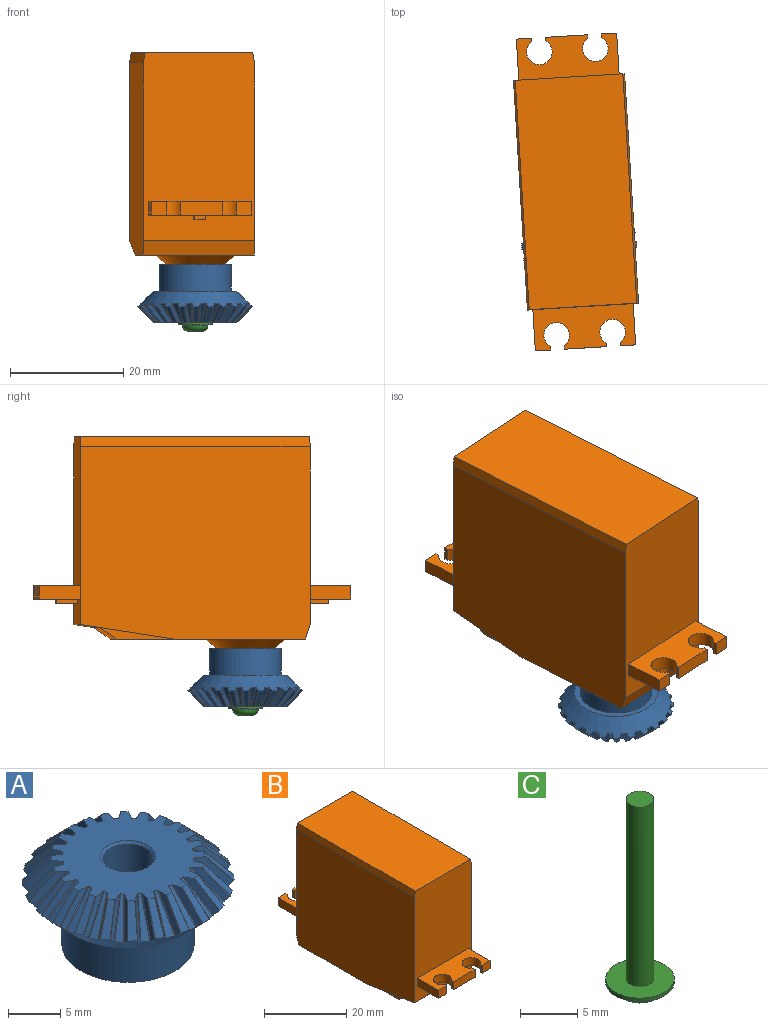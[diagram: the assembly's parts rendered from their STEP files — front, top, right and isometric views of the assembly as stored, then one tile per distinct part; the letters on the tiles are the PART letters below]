
ASSEMBLY  parts=3 mates=4
PART A: 200 faces, bbox 20.3x20.3x10.4 mm
  f0: cylinder r=0.05mm len=2.83mm, axis (0,-0.71,-0.71), area 0.2mm2, adj f1,f2,f181,f199
  f1: plane 3.76x3.28mm, normal (-0.94,-0.24,0.24), area 3.1mm2, adj f0,f3,f181,f199
  f2: cone r=10.16mm half-angle=45deg, axis (0,0,-1), area 3.1mm2, adj f0,f4,f181,f199
  f3: cylinder r=0.1mm len=3.37mm, axis (0,-0.71,-0.71), area 0.6mm2, adj f1,f5,f181,f199
  f4: cylinder r=0.05mm len=2.83mm, axis (-0.06,0.7,0.71), area 0.2mm2, adj f2,f6,f181,f199
  f5: cone r=5.83mm half-angle=45deg, axis (0,0,-1), area 2.7mm2, adj f3,f7,f181,f199
  f6: plane 3.77x3.28mm, normal (0.96,-0.16,0.24), area 3.1mm2, adj f4,f8,f181,f199
  f7: cylinder r=0.1mm len=3.37mm, axis (0.12,0.7,0.71), area 0.6mm2, adj f5,f9,f181,f199
  f8: cylinder r=0.1mm len=3.37mm, axis (-0.06,0.7,0.71), area 0.6mm2, adj f6,f10,f181,f199
  f9: plane 3.66x3.28mm, normal (0.88,-0.4,0.24), area 3.1mm2, adj f7,f11,f181,f199
  f10: cone r=5.83mm half-angle=45deg, axis (0,0,-1), area 2.7mm2, adj f8,f12,f181,f199
  f11: cylinder r=0.05mm len=2.83mm, axis (0.12,0.7,0.71), area 0.2mm2, adj f9,f13,f181,f199
  f12: cylinder r=0.1mm len=3.37mm, axis (0.18,-0.68,-0.71), area 0.6mm2, adj f10,f14,f181,f199
  f13: cone r=10.16mm half-angle=45deg, axis (0,0,-1), area 3.1mm2, adj f11,f15,f181,f199
  f14: plane 3.57x3.28mm, normal (-0.85,-0.48,0.24), area 3.1mm2, adj f12,f16,f181,f199
  f15: cylinder r=0.05mm len=2.83mm, axis (-0.18,-0.68,-0.71), area 0.2mm2, adj f13,f17,f181,f199
  f16: cylinder r=0.05mm len=2.83mm, axis (0.18,-0.68,-0.71), area 0.2mm2, adj f14,f18,f181,f199
  f17: plane 3.69x3.28mm, normal (-0.97,0.01,0.24), area 3.1mm2, adj f15,f19,f181,f199
  f18: cone r=10.16mm half-angle=45deg, axis (0,0,-1), area 3.1mm2, adj f16,f20,f181,f199
  f19: cylinder r=0.1mm len=3.37mm, axis (-0.18,-0.68,-0.71), area 0.6mm2, adj f17,f21,f181,f199
  f20: cylinder r=0.05mm len=2.83mm, axis (-0.24,0.66,0.71), area 0.2mm2, adj f18,f22,f181,f199
  f21: cone r=5.83mm half-angle=45deg, axis (0,0,-1), area 2.7mm2, adj f19,f23,f181,f199
  f22: plane 3.62x3.28mm, normal (0.97,0.09,0.24), area 3.1mm2, adj f20,f24,f181,f199
  f23: cylinder r=0.1mm len=3.37mm, axis (0.3,0.64,0.71), area 0.6mm2, adj f21,f25,f181,f199
  f24: cylinder r=0.1mm len=3.37mm, axis (-0.24,0.66,0.71), area 0.6mm2, adj f22,f26,f181,f199
  f25: plane 3.3x3.28mm, normal (0.75,-0.62,0.24), area 3.1mm2, adj f23,f27,f181,f199
  f26: cone r=5.83mm half-angle=45deg, axis (0,0,-1), area 2.7mm2, adj f24,f28,f181,f199
  f27: cylinder r=0.05mm len=2.83mm, axis (0.3,0.64,0.71), area 0.2mm2, adj f25,f29,f181,f199
  f28: cylinder r=0.1mm len=3.37mm, axis (0.35,-0.61,-0.71), area 0.6mm2, adj f26,f30,f181,f199
  f29: cone r=10.16mm half-angle=45deg, axis (0,0,-1), area 3.1mm2, adj f27,f31,f181,f199
  f30: plane 3.28x3.13mm, normal (-0.69,-0.68,0.24), area 3.1mm2, adj f28,f32,f181,f199
  f31: cylinder r=0.05mm len=2.83mm, axis (-0.35,-0.61,-0.71), area 0.2mm2, adj f29,f33,f181,f199
  f32: cylinder r=0.05mm len=2.83mm, axis (0.35,-0.61,-0.71), area 0.2mm2, adj f30,f34,f181,f199
  f33: plane 3.38x3.28mm, normal (-0.93,0.26,0.24), area 3.1mm2, adj f31,f35,f181,f199
  f34: cone r=10.16mm half-angle=45deg, axis (0,0,-1), area 3.1mm2, adj f32,f36,f181,f199
  f35: cylinder r=0.1mm len=3.37mm, axis (-0.35,-0.61,-0.71), area 0.6mm2, adj f33,f37,f181,f199
  f36: cylinder r=0.05mm len=2.83mm, axis (-0.41,0.58,0.71), area 0.2mm2, adj f34,f38,f181,f199
  f37: cone r=5.83mm half-angle=45deg, axis (0,0,-1), area 2.7mm2, adj f35,f39,f181,f199
  f38: plane 3.28x3.22mm, normal (0.91,0.34,0.24), area 3.1mm2, adj f36,f40,f181,f199
  f39: cylinder r=0.1mm len=3.37mm, axis (0.45,0.54,0.71), area 0.6mm2, adj f37,f41,f181,f199
  f40: cylinder r=0.1mm len=3.37mm, axis (-0.41,0.58,0.71), area 0.6mm2, adj f38,f42,f181,f199
  f41: plane 3.28x2.72mm, normal (0.56,-0.79,0.24), area 3.1mm2, adj f39,f43,f181,f199
  f42: cone r=5.83mm half-angle=45deg, axis (0,0,-1), area 2.7mm2, adj f40,f44,f181,f199
  f43: cylinder r=0.05mm len=2.83mm, axis (0.45,0.54,0.71), area 0.2mm2, adj f41,f45,f181,f199
  f44: cylinder r=0.1mm len=3.37mm, axis (0.5,-0.5,-0.71), area 0.6mm2, adj f42,f46,f181,f199
  f45: cone r=10.16mm half-angle=45deg, axis (0,0,-1), area 3.1mm2, adj f43,f47,f181,f199
  f46: plane 3.28x2.83mm, normal (-0.49,-0.84,0.24), area 3.1mm2, adj f44,f48,f181,f199
  f47: cylinder r=0.05mm len=2.83mm, axis (-0.5,-0.5,-0.71), area 0.2mm2, adj f45,f49,f181,f199
  f48: cylinder r=0.05mm len=2.83mm, axis (0.5,-0.5,-0.71), area 0.2mm2, adj f46,f50,f181,f199
  f49: plane 3.28x2.83mm, normal (-0.84,0.49,0.24), area 3.1mm2, adj f47,f51,f181,f199
  f50: cone r=10.16mm half-angle=45deg, axis (0,0,-1), area 3.1mm2, adj f48,f52,f181,f199
  f51: cylinder r=0.1mm len=3.37mm, axis (-0.5,-0.5,-0.71), area 0.6mm2, adj f49,f53,f181,f199
  f52: cylinder r=0.05mm len=2.83mm, axis (-0.54,0.45,0.71), area 0.2mm2, adj f50,f54,f181,f199
  f53: cone r=5.83mm half-angle=45deg, axis (0,0,-1), area 2.7mm2, adj f51,f55,f181,f199
  f54: plane 3.28x2.72mm, normal (0.79,0.56,0.24), area 3.1mm2, adj f52,f56,f181,f199
  f55: cylinder r=0.1mm len=3.37mm, axis (0.58,0.41,0.71), area 0.6mm2, adj f53,f57,f181,f199
  f56: cylinder r=0.1mm len=3.37mm, axis (-0.54,0.45,0.71), area 0.6mm2, adj f54,f58,f181,f199
  f57: plane 3.28x3.22mm, normal (0.34,-0.91,0.24), area 3.1mm2, adj f55,f59,f181,f199
  f58: cone r=5.83mm half-angle=45deg, axis (0,0,-1), area 2.7mm2, adj f56,f60,f181,f199
  f59: cylinder r=0.05mm len=2.83mm, axis (0.58,0.41,0.71), area 0.2mm2, adj f57,f61,f181,f199
  f60: cylinder r=0.1mm len=3.37mm, axis (0.61,-0.35,-0.71), area 0.6mm2, adj f58,f62,f181,f199
  f61: cone r=10.16mm half-angle=45deg, axis (0,0,-1), area 3.1mm2, adj f59,f63,f181,f199
  f62: plane 3.38x3.28mm, normal (-0.26,-0.93,0.24), area 3.1mm2, adj f60,f64,f181,f199
  f63: cylinder r=0.05mm len=2.83mm, axis (-0.61,-0.35,-0.71), area 0.2mm2, adj f61,f65,f181,f199
  f64: cylinder r=0.05mm len=2.83mm, axis (0.61,-0.35,-0.71), area 0.2mm2, adj f62,f66,f181,f199
  f65: plane 3.28x3.13mm, normal (-0.68,0.69,0.24), area 3.1mm2, adj f63,f67,f181,f199
  f66: cone r=10.16mm half-angle=45deg, axis (0,0,-1), area 3.1mm2, adj f64,f68,f181,f199
  f67: cylinder r=0.1mm len=3.37mm, axis (-0.61,-0.35,-0.71), area 0.6mm2, adj f65,f69,f181,f199
  f68: cylinder r=0.05mm len=2.83mm, axis (-0.64,0.3,0.71), area 0.2mm2, adj f66,f70,f181,f199
  f69: cone r=5.83mm half-angle=45deg, axis (0,0,-1), area 2.7mm2, adj f67,f71,f181,f199
  f70: plane 3.3x3.28mm, normal (0.62,0.75,0.24), area 3.1mm2, adj f68,f72,f181,f199
  f71: cylinder r=0.1mm len=3.37mm, axis (0.66,0.24,0.71), area 0.6mm2, adj f69,f73,f181,f199
  f72: cylinder r=0.1mm len=3.37mm, axis (-0.64,0.3,0.71), area 0.6mm2, adj f70,f74,f181,f199
  f73: plane 3.62x3.28mm, normal (0.09,-0.97,0.24), area 3.1mm2, adj f71,f75,f181,f199
  f74: cone r=5.83mm half-angle=45deg, axis (0,0,-1), area 2.7mm2, adj f72,f76,f181,f199
  f75: cylinder r=0.05mm len=2.83mm, axis (0.66,0.24,0.71), area 0.2mm2, adj f73,f77,f181,f199
  f76: cylinder r=0.1mm len=3.37mm, axis (0.68,-0.18,-0.71), area 0.6mm2, adj f74,f78,f181,f199
  f77: cone r=10.16mm half-angle=45deg, axis (0,0,-1), area 3.1mm2, adj f75,f79,f181,f199
  f78: plane 3.69x3.28mm, normal (-0.01,-0.97,0.24), area 3.1mm2, adj f76,f80,f181,f199
  f79: cylinder r=0.05mm len=2.83mm, axis (-0.68,-0.18,-0.71), area 0.2mm2, adj f77,f81,f181,f199
  f80: cylinder r=0.05mm len=2.83mm, axis (0.68,-0.18,-0.71), area 0.2mm2, adj f78,f82,f181,f199
  f81: plane 3.57x3.28mm, normal (-0.48,0.85,0.24), area 3.1mm2, adj f79,f83,f181,f199
  f82: cone r=10.16mm half-angle=45deg, axis (0,0,-1), area 3.1mm2, adj f80,f84,f181,f199
  f83: cylinder r=0.1mm len=3.37mm, axis (-0.68,-0.18,-0.71), area 0.6mm2, adj f81,f85,f181,f199
  f84: cylinder r=0.05mm len=2.83mm, axis (-0.7,0.12,0.71), area 0.2mm2, adj f82,f86,f181,f199
  f85: cone r=5.83mm half-angle=45deg, axis (0,0,-1), area 2.7mm2, adj f83,f87,f181,f199
  f86: plane 3.66x3.28mm, normal (0.4,0.88,0.24), area 3.1mm2, adj f84,f88,f181,f199
  f87: cylinder r=0.1mm len=3.37mm, axis (0.7,0.06,0.71), area 0.6mm2, adj f85,f89,f181,f199
  f88: cylinder r=0.1mm len=3.37mm, axis (-0.7,0.12,0.71), area 0.6mm2, adj f86,f90,f181,f199
  f89: plane 3.77x3.28mm, normal (-0.16,-0.96,0.24), area 3.1mm2, adj f87,f91,f181,f199
  f90: cone r=5.83mm half-angle=45deg, axis (0,0,-1), area 2.7mm2, adj f88,f92,f181,f199
  f91: cylinder r=0.05mm len=2.83mm, axis (0.7,0.06,0.71), area 0.2mm2, adj f89,f93,f181,f199
  f92: cylinder r=0.1mm len=3.37mm, axis (0.71,0,-0.71), area 0.6mm2, adj f90,f94,f181,f199
  f93: cone r=10.16mm half-angle=45deg, axis (0,0,-1), area 3.1mm2, adj f91,f95,f181,f199
  f94: plane 3.76x3.28mm, normal (0.24,-0.94,0.24), area 3.1mm2, adj f92,f96,f181,f199
  f95: cylinder r=0.05mm len=2.83mm, axis (-0.71,0,-0.71), area 0.2mm2, adj f93,f97,f181,f199
  f96: cylinder r=0.05mm len=2.83mm, axis (0.71,0,-0.71), area 0.2mm2, adj f94,f98,f181,f199
  f97: plane 3.76x3.28mm, normal (-0.24,0.94,0.24), area 3.1mm2, adj f95,f99,f181,f199
  f98: cone r=10.16mm half-angle=45deg, axis (0,0,-1), area 3.1mm2, adj f96,f100,f181,f199
  f99: cylinder r=0.1mm len=3.37mm, axis (-0.71,0,-0.71), area 0.6mm2, adj f97,f101,f181,f199
  f100: cylinder r=0.05mm len=2.83mm, axis (-0.7,-0.06,0.71), area 0.2mm2, adj f98,f102,f181,f199
  f101: cone r=5.83mm half-angle=45deg, axis (0,0,-1), area 2.7mm2, adj f99,f103,f181,f199
  f102: plane 3.77x3.28mm, normal (0.16,0.96,0.24), area 3.1mm2, adj f100,f104,f181,f199
  f103: cylinder r=0.1mm len=3.37mm, axis (0.7,-0.12,0.71), area 0.6mm2, adj f101,f105,f181,f199
  f104: cylinder r=0.1mm len=3.37mm, axis (-0.7,-0.06,0.71), area 0.6mm2, adj f102,f106,f181,f199
  f105: plane 3.66x3.28mm, normal (-0.4,-0.88,0.24), area 3.1mm2, adj f103,f107,f181,f199
  f106: cone r=5.83mm half-angle=45deg, axis (0,0,-1), area 2.7mm2, adj f104,f108,f181,f199
  f107: cylinder r=0.05mm len=2.83mm, axis (0.7,-0.12,0.71), area 0.2mm2, adj f105,f109,f181,f199
  f108: cylinder r=0.1mm len=3.37mm, axis (0.68,0.18,-0.71), area 0.6mm2, adj f106,f110,f181,f199
  f109: cone r=10.16mm half-angle=45deg, axis (0,0,-1), area 3.1mm2, adj f107,f111,f181,f199
  f110: plane 3.57x3.28mm, normal (0.48,-0.85,0.24), area 3.1mm2, adj f108,f112,f181,f199
  f111: cylinder r=0.05mm len=2.83mm, axis (-0.68,0.18,-0.71), area 0.2mm2, adj f109,f113,f181,f199
  f112: cylinder r=0.05mm len=2.83mm, axis (0.68,0.18,-0.71), area 0.2mm2, adj f110,f114,f181,f199
  f113: plane 3.69x3.28mm, normal (0.01,0.97,0.24), area 3.1mm2, adj f111,f115,f181,f199
  f114: cone r=10.16mm half-angle=45deg, axis (0,0,-1), area 3.1mm2, adj f112,f116,f181,f199
  f115: cylinder r=0.1mm len=3.37mm, axis (-0.68,0.18,-0.71), area 0.6mm2, adj f113,f117,f181,f199
  f116: cylinder r=0.05mm len=2.83mm, axis (-0.66,-0.24,0.71), area 0.2mm2, adj f114,f118,f181,f199
  f117: cone r=5.83mm half-angle=45deg, axis (0,0,-1), area 2.7mm2, adj f115,f119,f181,f199
  f118: plane 3.62x3.28mm, normal (-0.09,0.97,0.24), area 3.1mm2, adj f116,f120,f181,f199
  f119: cylinder r=0.1mm len=3.37mm, axis (0.64,-0.3,0.71), area 0.6mm2, adj f117,f121,f181,f199
  f120: cylinder r=0.1mm len=3.37mm, axis (-0.66,-0.24,0.71), area 0.6mm2, adj f118,f122,f181,f199
  f121: plane 3.3x3.28mm, normal (-0.62,-0.75,0.24), area 3.1mm2, adj f119,f123,f181,f199
  f122: cone r=5.83mm half-angle=45deg, axis (0,0,-1), area 2.7mm2, adj f120,f124,f181,f199
  f123: cylinder r=0.05mm len=2.83mm, axis (0.64,-0.3,0.71), area 0.2mm2, adj f121,f125,f181,f199
  f124: cylinder r=0.1mm len=3.37mm, axis (0.61,0.35,-0.71), area 0.6mm2, adj f122,f126,f181,f199
  f125: cone r=10.16mm half-angle=45deg, axis (0,0,-1), area 3.1mm2, adj f123,f127,f181,f199
  f126: plane 3.28x3.13mm, normal (0.68,-0.69,0.24), area 3.1mm2, adj f124,f128,f181,f199
  f127: cylinder r=0.05mm len=2.83mm, axis (-0.61,0.35,-0.71), area 0.2mm2, adj f125,f129,f181,f199
  f128: cylinder r=0.05mm len=2.83mm, axis (0.61,0.35,-0.71), area 0.2mm2, adj f126,f130,f181,f199
  f129: plane 3.38x3.28mm, normal (0.26,0.93,0.24), area 3.1mm2, adj f127,f131,f181,f199
  f130: cone r=10.16mm half-angle=45deg, axis (0,0,-1), area 3.1mm2, adj f128,f132,f181,f199
  f131: cylinder r=0.1mm len=3.37mm, axis (-0.61,0.35,-0.71), area 0.6mm2, adj f129,f133,f181,f199
  f132: cylinder r=0.05mm len=2.83mm, axis (-0.58,-0.41,0.71), area 0.2mm2, adj f130,f134,f181,f199
  f133: cone r=5.83mm half-angle=45deg, axis (0,0,-1), area 2.7mm2, adj f131,f135,f181,f199
  f134: plane 3.28x3.22mm, normal (-0.34,0.91,0.24), area 3.1mm2, adj f132,f136,f181,f199
  f135: cylinder r=0.1mm len=3.37mm, axis (0.54,-0.45,0.71), area 0.6mm2, adj f133,f137,f181,f199
  f136: cylinder r=0.1mm len=3.37mm, axis (-0.58,-0.41,0.71), area 0.6mm2, adj f134,f138,f181,f199
  f137: plane 3.28x2.72mm, normal (-0.79,-0.56,0.24), area 3.1mm2, adj f135,f139,f181,f199
  f138: cone r=5.83mm half-angle=45deg, axis (0,0,-1), area 2.7mm2, adj f136,f140,f181,f199
  f139: cylinder r=0.05mm len=2.83mm, axis (0.54,-0.45,0.71), area 0.2mm2, adj f137,f141,f181,f199
  f140: cylinder r=0.1mm len=3.37mm, axis (0.5,0.5,-0.71), area 0.6mm2, adj f138,f142,f181,f199
  f141: cone r=10.16mm half-angle=45deg, axis (0,0,-1), area 3.1mm2, adj f139,f143,f181,f199
  f142: plane 3.28x2.83mm, normal (0.84,-0.49,0.24), area 3.1mm2, adj f140,f144,f181,f199
  f143: cylinder r=0.05mm len=2.83mm, axis (-0.5,0.5,-0.71), area 0.2mm2, adj f141,f145,f181,f199
  f144: cylinder r=0.05mm len=2.83mm, axis (0.5,0.5,-0.71), area 0.2mm2, adj f142,f146,f181,f199
  f145: plane 3.28x2.83mm, normal (0.49,0.84,0.24), area 3.1mm2, adj f143,f147,f181,f199
  f146: cone r=10.16mm half-angle=45deg, axis (0,0,-1), area 3.1mm2, adj f144,f148,f181,f199
  f147: cylinder r=0.1mm len=3.37mm, axis (-0.5,0.5,-0.71), area 0.6mm2, adj f145,f149,f181,f199
  f148: cylinder r=0.05mm len=2.83mm, axis (-0.45,-0.54,0.71), area 0.2mm2, adj f146,f150,f181,f199
  f149: cone r=5.83mm half-angle=45deg, axis (0,0,-1), area 2.7mm2, adj f147,f151,f181,f199
  f150: plane 3.28x2.72mm, normal (-0.56,0.79,0.24), area 3.1mm2, adj f148,f152,f181,f199
  f151: cylinder r=0.1mm len=3.37mm, axis (0.41,-0.58,0.71), area 0.6mm2, adj f149,f153,f181,f199
  f152: cylinder r=0.1mm len=3.37mm, axis (-0.45,-0.54,0.71), area 0.6mm2, adj f150,f154,f181,f199
  f153: plane 3.28x3.22mm, normal (-0.91,-0.34,0.24), area 3.1mm2, adj f151,f155,f181,f199
  f154: cone r=5.83mm half-angle=45deg, axis (0,0,-1), area 2.7mm2, adj f152,f156,f181,f199
  f155: cylinder r=0.05mm len=2.83mm, axis (0.41,-0.58,0.71), area 0.2mm2, adj f153,f157,f181,f199
  f156: cylinder r=0.1mm len=3.37mm, axis (0.35,0.61,-0.71), area 0.6mm2, adj f154,f158,f181,f199
  f157: cone r=10.16mm half-angle=45deg, axis (0,0,-1), area 3.1mm2, adj f155,f159,f181,f199
  f158: plane 3.38x3.28mm, normal (0.93,-0.26,0.24), area 3.1mm2, adj f156,f160,f181,f199
  f159: cylinder r=0.05mm len=2.83mm, axis (-0.35,0.61,-0.71), area 0.2mm2, adj f157,f161,f181,f199
  f160: cylinder r=0.05mm len=2.83mm, axis (0.35,0.61,-0.71), area 0.2mm2, adj f158,f162,f181,f199
  f161: plane 3.28x3.13mm, normal (0.69,0.68,0.24), area 3.1mm2, adj f159,f163,f181,f199
  f162: cone r=10.16mm half-angle=45deg, axis (0,0,-1), area 3.1mm2, adj f160,f164,f181,f199
  f163: cylinder r=0.1mm len=3.37mm, axis (-0.35,0.61,-0.71), area 0.6mm2, adj f161,f165,f181,f199
  f164: cylinder r=0.05mm len=2.83mm, axis (-0.3,-0.64,0.71), area 0.2mm2, adj f162,f166,f181,f199
  f165: cone r=5.83mm half-angle=45deg, axis (0,0,-1), area 2.7mm2, adj f163,f167,f181,f199
  f166: plane 3.3x3.28mm, normal (-0.75,0.62,0.24), area 3.1mm2, adj f164,f168,f181,f199
  f167: cylinder r=0.1mm len=3.37mm, axis (0.24,-0.66,0.71), area 0.6mm2, adj f165,f169,f181,f199
  f168: cylinder r=0.1mm len=3.37mm, axis (-0.3,-0.64,0.71), area 0.6mm2, adj f166,f170,f181,f199
  f169: plane 3.62x3.28mm, normal (-0.97,-0.09,0.24), area 3.1mm2, adj f167,f171,f181,f199
  f170: cone r=5.83mm half-angle=45deg, axis (0,0,-1), area 2.7mm2, adj f168,f172,f181,f199
  f171: cylinder r=0.05mm len=2.83mm, axis (0.24,-0.66,0.71), area 0.2mm2, adj f169,f173,f181,f199
  f172: cylinder r=0.1mm len=3.37mm, axis (0.18,0.68,-0.71), area 0.6mm2, adj f170,f174,f181,f199
  f173: cone r=10.16mm half-angle=45deg, axis (0,0,-1), area 3.1mm2, adj f171,f175,f181,f199
  f174: plane 3.69x3.28mm, normal (0.97,-0.01,0.24), area 3.1mm2, adj f172,f176,f181,f199
  f175: cylinder r=0.05mm len=2.83mm, axis (-0.18,0.68,-0.71), area 0.2mm2, adj f173,f177,f181,f199
  f176: cylinder r=0.05mm len=2.83mm, axis (0.18,0.68,-0.71), area 0.2mm2, adj f174,f178,f181,f199
  f177: plane 3.57x3.28mm, normal (0.85,0.48,0.24), area 3.1mm2, adj f175,f179,f181,f199
  f178: cone r=10.16mm half-angle=45deg, axis (0,0,-1), area 3.1mm2, adj f176,f180,f181,f199
  f179: cylinder r=0.1mm len=3.37mm, axis (-0.18,0.68,-0.71), area 0.6mm2, adj f177,f181,f182,f199
  f180: cylinder r=0.05mm len=2.83mm, axis (-0.12,-0.7,0.71), area 0.2mm2, adj f178,f181,f183,f199
  f181: cone r=10.16mm half-angle=45deg, axis (0,0,1), area 192.1mm2, adj f0,f1,f2,f3,f4,f5,f6,f7
  f182: cone r=5.83mm half-angle=45deg, axis (0,0,-1), area 2.7mm2, adj f179,f181,f185,f199
  f183: plane 3.66x3.28mm, normal (-0.88,0.4,0.24), area 3.1mm2, adj f180,f181,f186,f199
  f184: plane 14.76x14.76mm, normal (0,0,-1), area 44.5mm2, adj f181,f187
  f185: cylinder r=0.1mm len=3.37mm, axis (0.06,-0.7,0.71), area 0.6mm2, adj f181,f182,f188,f199
  f186: cylinder r=0.1mm len=3.37mm, axis (-0.12,-0.7,0.71), area 0.6mm2, adj f181,f183,f189,f199
  f187: cylinder r=6.35mm len=12.7mm, axis (0,0,1), area 190mm2, adj f184,f190
  f188: plane 3.77x3.28mm, normal (-0.96,0.16,0.24), area 3.1mm2, adj f181,f185,f191,f199
  f189: cone r=5.83mm half-angle=45deg, axis (0,0,-1), area 2.7mm2, adj f181,f186,f192,f199
  f190: plane 12.7x12.7mm, normal (0,0,-1), area 105mm2, adj f187,f193
  f191: cylinder r=0.05mm len=2.83mm, axis (0.06,-0.7,0.71), area 0.2mm2, adj f181,f188,f194,f199
  f192: cylinder r=0.1mm len=3.37mm, axis (0,0.71,-0.71), area 0.6mm2, adj f181,f189,f195,f199
  f193: cone r=2.63mm half-angle=45deg, axis (0,0,-1), area 5.6mm2, adj f190,f196
  f194: cone r=10.16mm half-angle=45deg, axis (0,0,-1), area 3.1mm2, adj f181,f191,f197,f199
  f195: plane 3.76x3.28mm, normal (0.94,0.24,0.24), area 3.1mm2, adj f181,f192,f197,f199
  f196: cylinder r=2.37mm len=9.81mm, axis (0,0,-1), area 146.4mm2, adj f193,f198
  f197: cylinder r=0.05mm len=2.83mm, axis (0,0.71,-0.71), area 0.2mm2, adj f181,f194,f195,f199
  f198: cone r=2.63mm half-angle=45deg, axis (0,0,1), area 5.6mm2, adj f196,f199
  f199: plane 14.79x14.79mm, normal (0,0,1), area 128.5mm2, adj f0,f1,f2,f3,f4,f5,f6,f7
PART B: 51 faces, bbox 19.7x55.3x37.4 mm
  f0: plane 17.78x7.32mm, normal (0,0,-1), area 89.1mm2, adj f2,f3,f4,f12,f39,f40,f41,f42
  f1: plane 17.78x7.32mm, normal (0,0,1), area 96.4mm2, adj f2,f3,f4,f12,f39,f40,f41,f42
  f2: plane 2.71x2.41mm, normal (0,-1,0), area 6.5mm2, adj f0,f1,f40,f44
  f3: plane 7.49x2.41mm, normal (0,-1,0), area 18.1mm2, adj f0,f1,f41,f46
  f4: plane 2.71x2.41mm, normal (0,-1,0), area 6.5mm2, adj f0,f1,f39,f43
  f5: plane 33.22x19.69mm, normal (0,1,0), area 608.9mm2, adj f6,f11,f13,f14,f15,f16,f21,f25
  f6: plane 17.78x7.32mm, normal (0,0,-1), area 89.1mm2, adj f5,f7,f8,f25,f27,f28,f29,f30
  f7: plane 2.71x2.41mm, normal (0,1,0), area 6.5mm2, adj f6,f26,f27,f32
  f8: plane 7.49x2.41mm, normal (0,1,0), area 18.1mm2, adj f6,f26,f29,f33
  f9: plane 33.49x19.69mm, normal (0,0,-1), area 479.4mm2, adj f10,f11,f13,f17,f18,f19,f21,f22
  f10: plane 19.69x16.51mm, normal (0,-0.15,-0.99), area 92.1mm2, adj f9,f11,f12,f13,f17,f18,f19
  f11: plane 40.64x33.99mm, normal (-1,0,0), area 1358.9mm2, adj f5,f9,f10,f12,f16,f21
  f12: plane 33.19x19.69mm, normal (0,-1,0), area 608.3mm2, adj f0,f1,f10,f11,f13,f14,f15,f16
  f13: plane 40.64x33.99mm, normal (1,0,0), area 1358.9mm2, adj f5,f9,f10,f12,f15,f21
  f14: plane 40.64x19.06mm, normal (0,0,1), area 774.5mm2, adj f5,f12,f15,f16
  f15: plane 40.64x1.78mm, normal (0.98,0,0.17), area 73.4mm2, adj f5,f12,f13,f14
  f16: plane 40.64x1.78mm, normal (-0.98,0,0.17), area 73.4mm2, adj f5,f11,f12,f14
  f17: plane 13.07x2.03mm, normal (-1,0,0), area 10.3mm2, adj f9,f10,f19
  f18: plane 13.07x2.03mm, normal (1,0,0), area 10.3mm2, adj f9,f10,f19
  f19: plane 17.91x2.91mm, normal (0,-0.57,-0.82), area 63.5mm2, adj f9,f10,f17,f18
  f20: plane 10.16x10.16mm, normal (0,0,-1), area 53.6mm2, adj f22,f23
  f21: plane 19.69x2.54mm, normal (0,0.95,-0.3), area 52.4mm2, adj f5,f9,f11,f13
  f22: cone r=5.08mm half-angle=52.2deg, axis (0,0,1), area 102.1mm2, adj f9,f20
  f23: cylinder r=2.96mm len=10mm, axis (0,0,-1), area 185.9mm2, adj f20,f24
  f24: plane 5.92x5.92mm, normal (0,0,-1), area 27.5mm2, adj f23
  f25: plane 7.32x2.41mm, normal (-1,0,0), area 17.7mm2, adj f5,f6,f26,f28
  f26: plane 17.78x7.32mm, normal (0,0,1), area 96.4mm2, adj f5,f7,f8,f25,f27,f28,f29,f30
  f27: plane 7.32x2.41mm, normal (1,0,0), area 17.7mm2, adj f5,f6,f7,f26
  f28: plane 2.71x2.41mm, normal (0,1,0), area 6.5mm2, adj f6,f25,f26,f30
  f29: plane 2.41x0.64mm, normal (-1,0,0), area 1.5mm2, adj f6,f8,f26,f31
  f30: plane 2.41x0.64mm, normal (1,0,0), area 1.5mm2, adj f6,f26,f28,f31
  f31: cylinder r=2.25mm len=4.5mm, axis (0,0,-1), area 27.9mm2, adj f6,f26,f29,f30
  f32: plane 2.41x0.64mm, normal (-1,0,0), area 1.5mm2, adj f6,f7,f26,f34
  f33: plane 2.41x0.64mm, normal (1,0,0), area 1.5mm2, adj f6,f8,f26,f34
  f34: cylinder r=2.25mm len=4.5mm, axis (0,0,-1), area 27.9mm2, adj f6,f26,f32,f33
  f35: plane 3.81x0.86mm, normal (1,0,0), area 3.3mm2, adj f5,f6,f37,f38
  f36: plane 3.81x0.86mm, normal (-1,0,0), area 3.3mm2, adj f5,f6,f37,f38
  f37: plane 1.91x0.86mm, normal (0,1,0), area 1.6mm2, adj f6,f35,f36,f38
  f38: plane 3.81x1.91mm, normal (0,0,-1), area 7.3mm2, adj f5,f35,f36,f37
  f39: plane 7.32x2.41mm, normal (-1,0,0), area 17.7mm2, adj f0,f1,f4,f12
  f40: plane 7.32x2.41mm, normal (1,0,0), area 17.7mm2, adj f0,f1,f2,f12
  f41: plane 2.41x0.64mm, normal (-1,0,0), area 1.5mm2, adj f0,f1,f3,f42
  f42: cylinder r=2.25mm len=4.5mm, axis (0,0,-1), area 27.9mm2, adj f0,f1,f41,f43
  f43: plane 2.41x0.64mm, normal (1,0,0), area 1.5mm2, adj f0,f1,f4,f42
  f44: plane 2.41x0.64mm, normal (-1,0,0), area 1.5mm2, adj f0,f1,f2,f45
  f45: cylinder r=2.25mm len=4.5mm, axis (0,0,-1), area 27.9mm2, adj f0,f1,f44,f46
  f46: plane 2.41x0.64mm, normal (1,0,0), area 1.5mm2, adj f0,f1,f3,f45
  f47: plane 3.81x0.86mm, normal (1,0,0), area 3.3mm2, adj f0,f12,f48,f50
  f48: plane 1.91x0.86mm, normal (0,-1,0), area 1.6mm2, adj f0,f47,f49,f50
  f49: plane 3.81x0.86mm, normal (-1,0,0), area 3.3mm2, adj f0,f12,f48,f50
  f50: plane 3.81x1.91mm, normal (0,0,-1), area 7.3mm2, adj f12,f47,f48,f49
PART C: 8 faces, bbox 6x6x20.7 mm
  f0: plane 5.97x5.97mm, normal (0,0,-1), area 12.1mm2, adj f4,f5
  f1: cylinder r=1.22mm len=19.14mm, axis (0,0,-1), area 146.7mm2, adj f2,f3
  f2: plane 2.44x2.44mm, normal (0,0,1), area 4.7mm2, adj f1
  f3: plane 5.97x5.97mm, normal (0,0,1), area 23.3mm2, adj f1,f4
  f4: cylinder r=2.98mm len=5.97mm, axis (0,0,1), area 7.1mm2, adj f0,f3
  f5: cylinder r=2.25mm len=4.5mm, axis (0,0,1), area 1.8mm2, adj f0,f7
  f6: plane 2.46x2.46mm, normal (0,0,-1), area 4.8mm2, adj f7
  f7: torus R=1.23mm, axis (0,0,-1), area 18.8mm2, adj f5,f6
PLACE A rot(axis=(1,0.03,0),180deg) t=(1.4,9.73,-39.08)mm
PLACE B rot(axis=(0,0,-1),176.5deg) t=(0.83,19.17,-32.3)mm
PLACE C rot(axis=(0,0,-1),86.5deg) t=(1.4,9.73,-44.24)mm
MATE planar A.f2 <-> B.f22  axis (0,0,1) through (1.4,9.73,-33.92)mm
MATE slider C.f1 <-> A.f2  axis (0,0,-1) through (1.4,9.73,-34.67)mm
MATE cylindrical B.f22 <-> C.f1  axis (0,0,-1) through (1.4,9.73,-23.92)mm
MATE planar C.f1 <-> A.f85  axis (0,0,1) through (1.4,9.73,-44.24)mm
